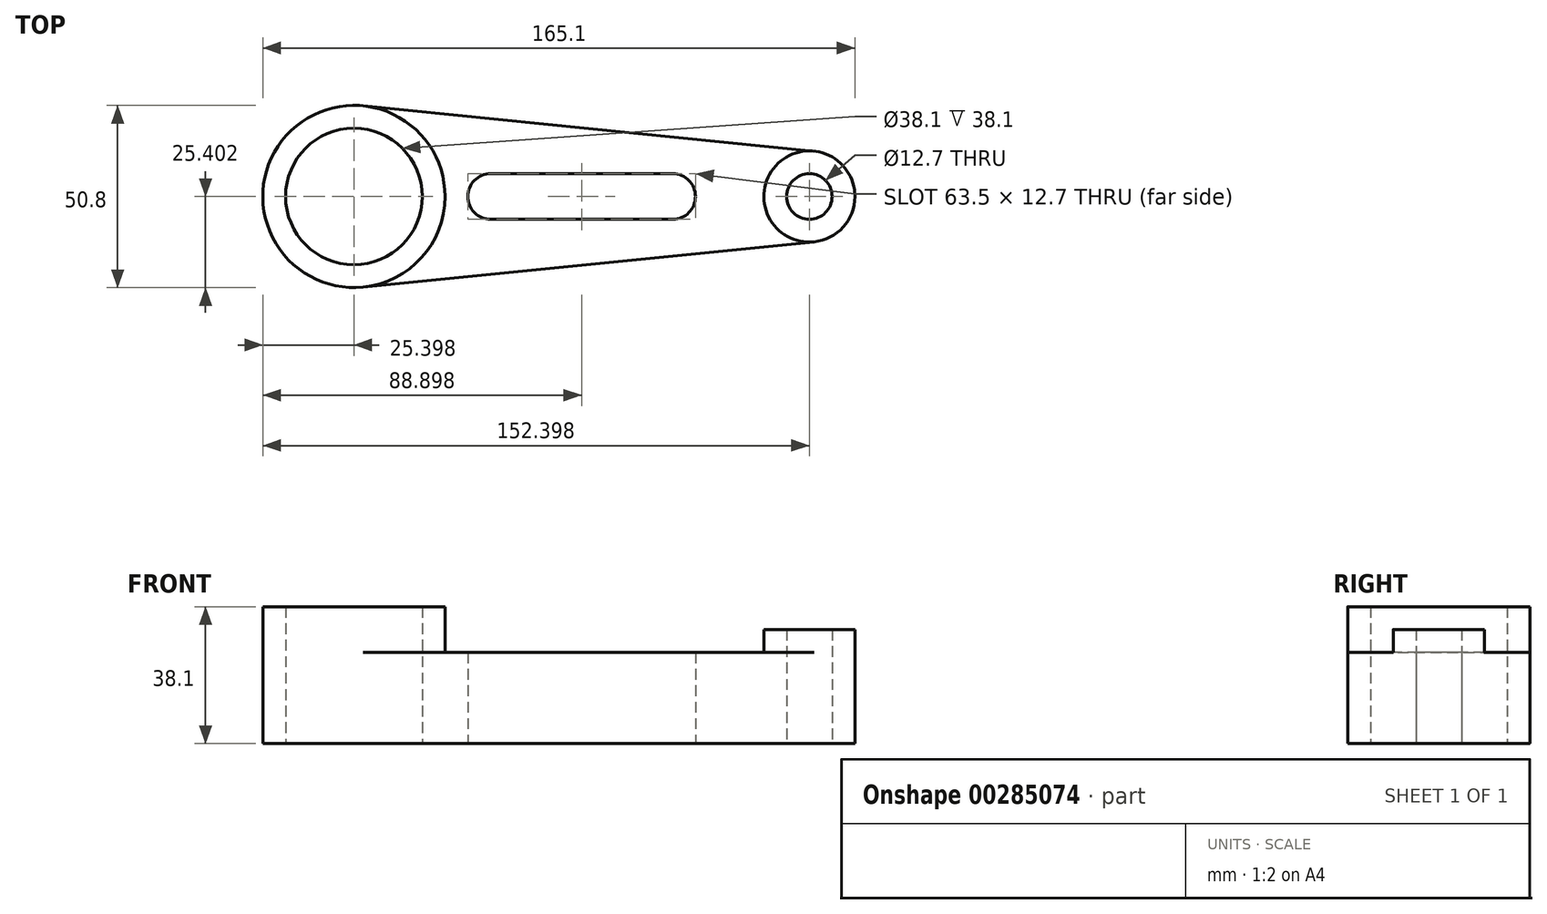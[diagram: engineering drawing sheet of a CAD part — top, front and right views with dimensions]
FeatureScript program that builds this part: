
annotation { "Feature Type Name" : "Feature", "Feature Type Description" : "" }
export const myFeature = defineFeature(function(context is Context, id is Id, definition is map)
    precondition{}
    {
        {
            var Q0;
            Q0=qCreatedBy(makeId("Top.planeOp"),FACE);
            var sketch = newSketch(context, id + "F0", { "sketchPlane" : qUnion([Q0])});
            skLineSegment(sketch, "E0.bottom", {"start": v(166.16, 19.13) * mm, "end": v(216.96, 19.13) * mm});
            skLineSegment(sketch, "E0.top", {"start": v(166.16, 6.43) * mm, "end": v(216.96, 6.43) * mm});
            skCircle(sketch, "E1", {"center": v(255.06, 12.78) * mm, "radius": 6.35 * mm});
            skCircle(sketch, "E2", {"center": v(255.06, 12.78) * mm, "radius": 12.7 * mm});
            skCircle(sketch, "E3", {"center": v(128.06, 12.78) * mm, "radius": 25.4 * mm});
            skCircle(sketch, "E4", {"center": v(128.06, 12.78) * mm, "radius": 19.05 * mm});
            skArc(sketch, "E5", {"start": v(166.16, 19.13) * mm, "mid": v(159.8, 12.78) * mm, "end": v(166.16, 6.43) * mm});
            skArc(sketch, "E6", {"start": v(216.96, 6.43) * mm, "mid": v(223.3, 12.78) * mm, "end": v(216.96, 19.13) * mm});
            skLineSegment(sketch, "E7", {"start": v(130.6, 38.05) * mm, "end": v(256.33, 25.42) * mm});
            skLineSegment(sketch, "E8", {"start": v(130.6, -12.5) * mm, "end": v(256.33, 0.15) * mm});
            skSolve(sketch);
        }
        {
            var Q0;
            Q0=makeQuery(id+"F0.imprint","IMPRINT",FACE,{"disambiguationData":[TD([[makeQuery(id+"F0.imprint","IMPRINT",EDGE,{"derivedFrom":sQuery(id+"F0.wireOp",EDGE,"E0.bottom")}),1.0]])]});
            extrude(context, id + "F1", {"entities" : qUnion([Q0]), "depth" : 25.4 * mm});
        }
        {
            var Q0;
            Q0=makeQuery(id+"F0.imprint","IMPRINT",FACE,{"disambiguationData":[TD([[makeQuery(id+"F0.imprint","IMPRINT",EDGE,{"derivedFrom":sQuery(id+"F0.wireOp",EDGE,"E4")}),-1.0]])]});
            extrude(context, id + "F2", {"entities" : qUnion([Q0]), "operationType" : NewBodyOperationType.ADD, "depth" : 38.1 * mm});
        }
        {
            var Q0;
            Q0=makeQuery(id+"F0.imprint","IMPRINT",FACE,{"disambiguationData":[TD([[makeQuery(id+"F0.imprint","IMPRINT",EDGE,{"derivedFrom":sQuery(id+"F0.wireOp",EDGE,"E1")}),-1.0]])]});
            extrude(context, id + "F3", {"entities" : qUnion([Q0]), "operationType" : NewBodyOperationType.ADD, "depth" : 31.75 * mm});
        }
    });
